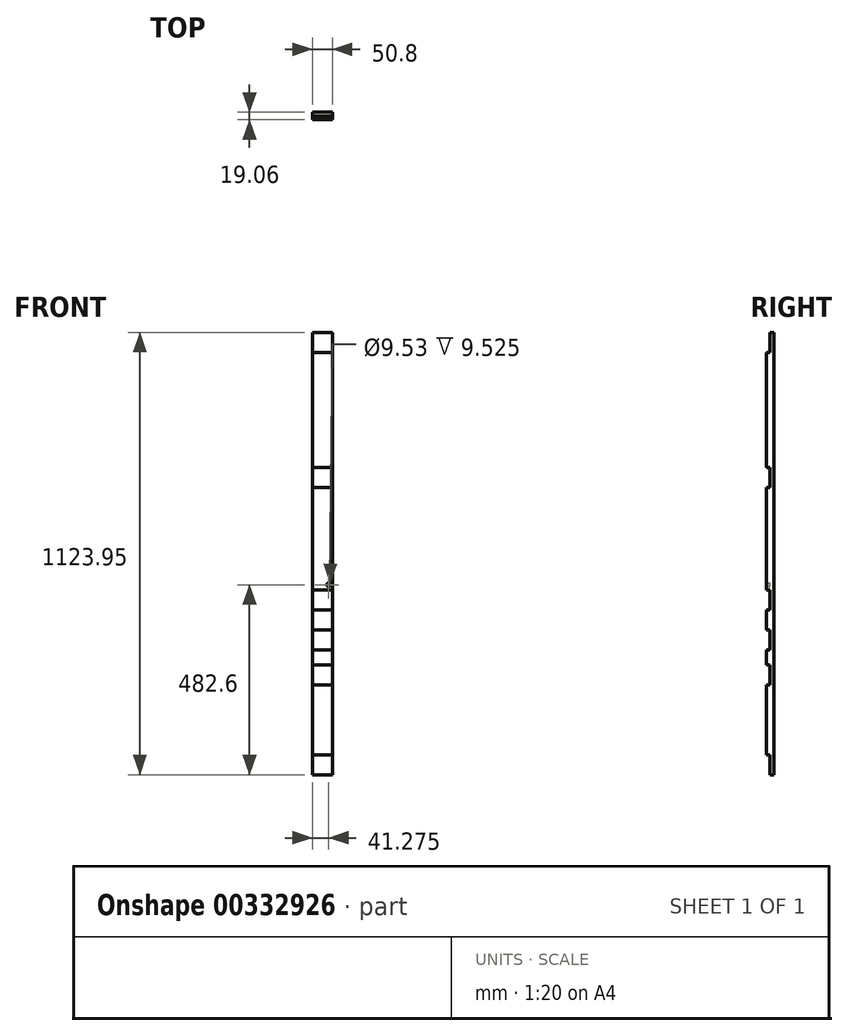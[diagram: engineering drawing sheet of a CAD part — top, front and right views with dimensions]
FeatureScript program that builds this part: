
annotation { "Feature Type Name" : "Feature", "Feature Type Description" : "" }
export const myFeature = defineFeature(function(context is Context, id is Id, definition is map)
    precondition{}
    {
        {
            var Q0;
            Q0=qCreatedBy(makeId("Top.planeOp"),FACE);
            var sketch = newSketch(context, id + "F0", { "sketchPlane" : qUnion([Q0])});
            skLineSegment(sketch, "E0.bottom", {"start": v(25.4, 9.53) * mm, "end": v(-25.4, 9.53) * mm});
            skLineSegment(sketch, "E0.top", {"start": v(25.4, -9.53) * mm, "end": v(-25.4, -9.53) * mm});
            skLineSegment(sketch, "E0.left", {"start": v(25.4, 9.53) * mm, "end": v(25.4, -9.52) * mm});
            skLineSegment(sketch, "E0.right", {"start": v(-25.4, 9.53) * mm, "end": v(-25.4, -9.53) * mm});
            skPoint(sketch, "E0.middle", {"position": v(0, 0) * mm});
            skSolve(sketch);
        }
        {
            var Q0;
            Q0=makeQuery(id+"F0.imprint","IMPRINT",FACE,{"disambiguationData":[TD([[makeQuery(id+"F0.imprint","IMPRINT",EDGE,{"derivedFrom":sQuery(id+"F0.wireOp",EDGE,"E0.bottom")}),1.0]])]});
            extrude(context, id + "F1", {"entities" : qUnion([Q0]), "depth" : 1123.95 * mm});
        }
        {
            var Q0;
            Q0=qCreatedBy(makeId("Front.planeOp"),FACE);
            var sketch = newSketch(context, id + "F2", { "sketchPlane" : qUnion([Q0])});
            skLineSegment(sketch, "E1.bottom", {"start": v(-38.77, 0) * mm, "end": v(83.66, 0) * mm});
            skLineSegment(sketch, "E1.top", {"start": v(-38.77, 50.8) * mm, "end": v(83.66, 50.8) * mm});
            skLineSegment(sketch, "E1.left", {"start": v(-38.77, 0) * mm, "end": v(-38.77, 50.8) * mm});
            skLineSegment(sketch, "E1.right", {"start": v(83.66, 0) * mm, "end": v(83.66, 50.8) * mm});
            skLineSegment(sketch, "E2.bottom", {"start": v(-59.18, 317.5) * mm, "end": v(49.65, 317.5) * mm});
            skLineSegment(sketch, "E2.top", {"start": v(-59.18, 368.3) * mm, "end": v(49.65, 368.3) * mm});
            skLineSegment(sketch, "E2.left", {"start": v(-59.18, 317.5) * mm, "end": v(-59.18, 368.3) * mm});
            skLineSegment(sketch, "E2.right", {"start": v(49.65, 317.5) * mm, "end": v(49.65, 368.3) * mm});
            skLineSegment(sketch, "E3.bottom", {"start": v(-44.21, 730.25) * mm, "end": v(49.65, 730.25) * mm});
            skLineSegment(sketch, "E3.top", {"start": v(-44.21, 781.05) * mm, "end": v(49.65, 781.05) * mm});
            skLineSegment(sketch, "E3.left", {"start": v(-44.21, 730.25) * mm, "end": v(-44.21, 781.05) * mm});
            skLineSegment(sketch, "E3.right", {"start": v(49.65, 730.25) * mm, "end": v(49.65, 781.05) * mm});
            skLineSegment(sketch, "E4.bottom", {"start": v(-74.14, 469.9) * mm, "end": v(71.42, 469.9) * mm});
            skLineSegment(sketch, "E4.top", {"start": v(-74.14, 419.1) * mm, "end": v(71.42, 419.1) * mm});
            skLineSegment(sketch, "E4.left", {"start": v(-74.14, 469.9) * mm, "end": v(-74.14, 419.1) * mm});
            skLineSegment(sketch, "E4.right", {"start": v(71.42, 469.9) * mm, "end": v(71.42, 419.1) * mm});
            skLineSegment(sketch, "E5.bottom", {"start": v(-210.36, 1073.15) * mm, "end": v(132.8, 1073.15) * mm});
            skLineSegment(sketch, "E5.top", {"start": v(-210.36, 1123.95) * mm, "end": v(132.8, 1123.95) * mm});
            skLineSegment(sketch, "E5.left", {"start": v(-210.36, 1073.15) * mm, "end": v(-210.36, 1123.95) * mm});
            skLineSegment(sketch, "E5.right", {"start": v(132.8, 1073.15) * mm, "end": v(132.8, 1123.95) * mm});
            skLineSegment(sketch, "E6.bottom", {"start": v(-145.57, 228.6) * mm, "end": v(93.98, 228.6) * mm});
            skLineSegment(sketch, "E6.top", {"start": v(-145.57, 279.4) * mm, "end": v(93.98, 279.4) * mm});
            skLineSegment(sketch, "E6.left", {"start": v(-145.57, 228.6) * mm, "end": v(-145.57, 279.4) * mm});
            skLineSegment(sketch, "E6.right", {"start": v(93.98, 228.6) * mm, "end": v(93.98, 279.4) * mm});
            skSolve(sketch);
        }
        {
            var Q0;
            Q0=qSketchRegion(id+"F2",true);
            extrude(context, id + "F3", {"entities" : qUnion([Q0]), "operationType" : NewBodyOperationType.REMOVE, "depth" : 25.4 * mm});
        }
        {
            var Q0;
            Q0=qCreatedBy(makeId("Front.planeOp"),FACE);
            var sketch = newSketch(context, id + "F4", { "sketchPlane" : qUnion([Q0])});
            skCircle(sketch, "E7", {"center": v(15.88, 254) * mm, "radius": 4.76 * mm});
            skCircle(sketch, "E8", {"center": v(15.87, 482.6) * mm, "radius": 4.76 * mm});
            skSolve(sketch);
        }
        {
            var Q0;
            Q0 = qSketchRegion(id + "F4", true);
            extrude(context, id + "F5", {"entities" : qUnion([Q0]), "operationType" : NewBodyOperationType.REMOVE, "depth" : 25.4 * mm});
        }
    });
